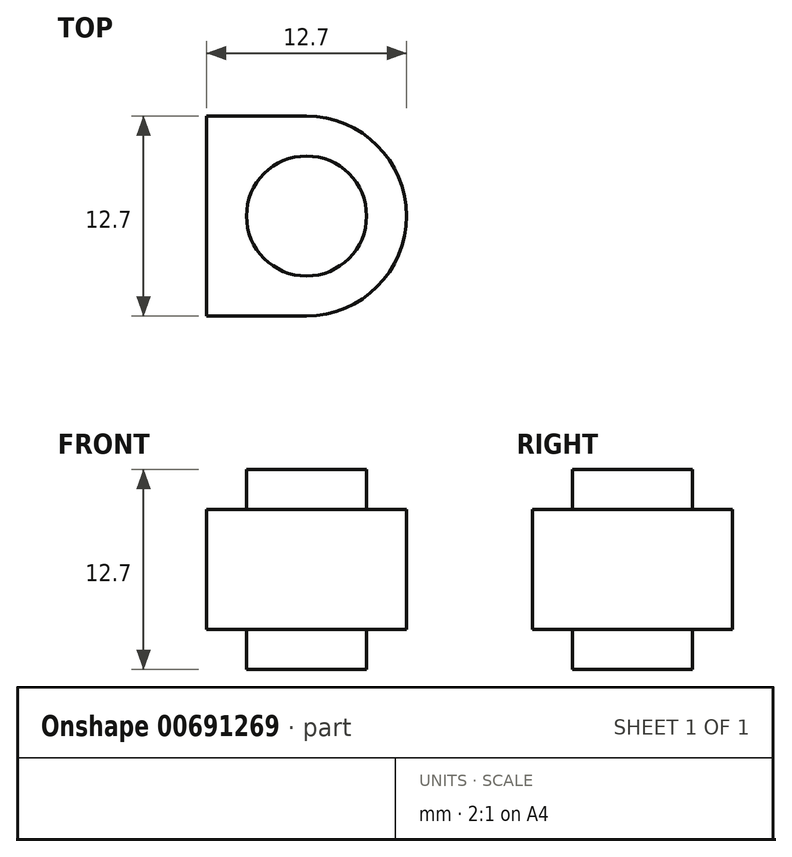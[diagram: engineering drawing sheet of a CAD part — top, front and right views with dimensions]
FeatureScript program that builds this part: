
annotation { "Feature Type Name" : "Feature", "Feature Type Description" : "" }
export const myFeature = defineFeature(function(context is Context, id is Id, definition is map)
    precondition{}
    {
        {
            var Q0;
            Q0=qCreatedBy(makeId("Top.planeOp"),FACE);
            var sketch = newSketch(context, id + "F0", { "sketchPlane" : qUnion([Q0])});
            skLineSegment(sketch, "E0", {"start": v(0, 0) * mm, "end": v(0, 12.7) * mm});
            skCircle(sketch, "E1", {"center": v(0, 6.35) * mm, "radius": 6.35 * mm});
            skLineSegment(sketch, "E2", {"start": v(0, 12.7) * mm, "end": v(-6.35, 12.7) * mm});
            skLineSegment(sketch, "E3", {"start": v(-6.35, 12.7) * mm, "end": v(-6.35, 0) * mm});
            skLineSegment(sketch, "E4", {"start": v(-6.35, 0) * mm, "end": v(0, 0) * mm});
            skSolve(sketch);
        }
        {
            var Q0;
            Q0 = qSketchRegion(id + "F0", true);
            extrude(context, id + "F1", {"entities" : qUnion([Q0]), "depth" : 7.62 * mm, "offsetDistance" : 25.4 * mm});
        }
        {
            var Q0;
            Q0=makeQuery(id+"F1.opExtrude","CAP_FACE",FACE,{"disambiguationData":[OSD([sQuery(id+"F0.wireOp",EDGE,"E1"),sQuery(id+"F0.wireOp",EDGE,"E2"),sQuery(id+"F0.wireOp",EDGE,"E3"),sQuery(id+"F0.wireOp",EDGE,"E4")])],"isStart":false});
            var sketch = newSketch(context, id + "F2", { "sketchPlane" : qUnion([Q0])});
            skLineSegment(sketch, "E5", {"start": v(0, 0) * mm, "end": v(0, 12.7) * mm});
            skCircle(sketch, "E6", {"center": v(0, 6.35) * mm, "radius": 3.81 * mm});
            skSolve(sketch);
        }
        {
            var Q0;
            Q0 = qSketchRegion(id + "F2", true);
            extrude(context, id + "F3", {"entities" : qUnion([Q0]), "operationType" : NewBodyOperationType.ADD, "depth" : 2.54 * mm, "offsetDistance" : 25.4 * mm});
        }
        {
            var Q0;
            Q0=makeQuery(id+"F1.opExtrude","CAP_FACE",FACE,{"disambiguationData":[OSD([sQuery(id+"F0.wireOp",EDGE,"E1"),sQuery(id+"F0.wireOp",EDGE,"E2"),sQuery(id+"F0.wireOp",EDGE,"E3"),sQuery(id+"F0.wireOp",EDGE,"E4")])],"isStart":true});
            var sketch = newSketch(context, id + "F4", { "sketchPlane" : qUnion([Q0])});
            skLineSegment(sketch, "E7", {"start": v(0, -12.7) * mm, "end": v(0, 0) * mm});
            skCircle(sketch, "E8", {"center": v(0, -6.35) * mm, "radius": 3.81 * mm});
            skPoint(sketch, "E8.perimeterSnap0", {"position": v(0, -6.35) * mm});
            skSolve(sketch);
        }
        {
            var Q0;
            Q0 = qSketchRegion(id + "F4", true);
            extrude(context, id + "F5", {"entities" : qUnion([Q0]), "operationType" : NewBodyOperationType.ADD, "depth" : 2.54 * mm, "offsetDistance" : 25.4 * mm});
        }
    });
